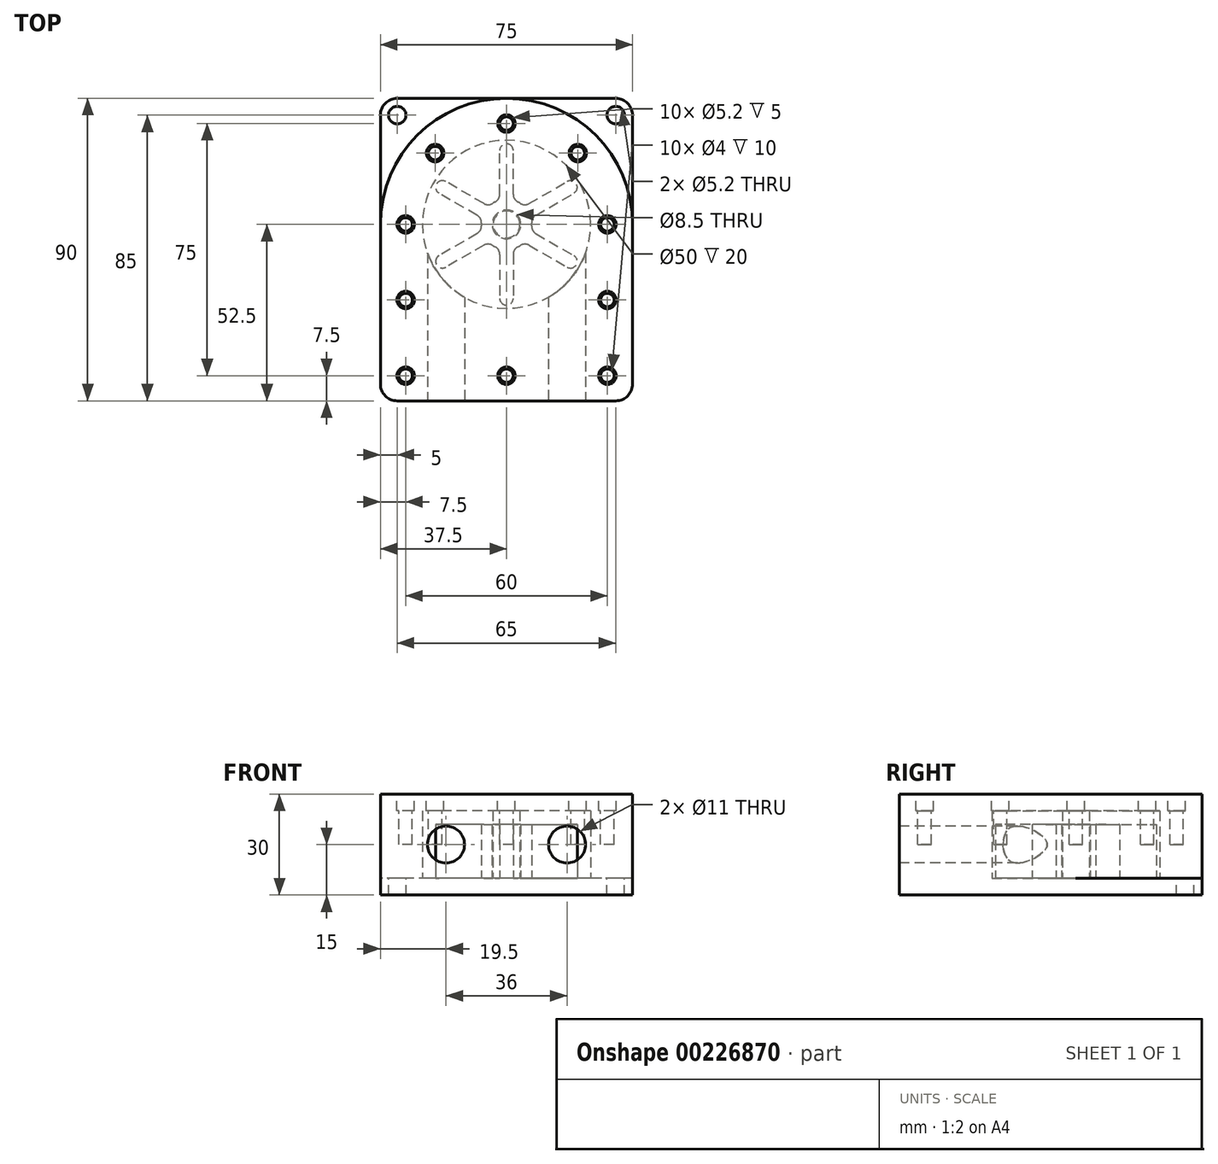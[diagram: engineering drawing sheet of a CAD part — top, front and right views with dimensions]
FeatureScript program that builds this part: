
annotation { "Feature Type Name" : "Feature", "Feature Type Description" : "" }
export const myFeature = defineFeature(function(context is Context, id is Id, definition is map)
    precondition{}
    {
        {
            var Q0;
            Q0=qCreatedBy(makeId("Top.planeOp"),FACE);
            var sketch = newSketch(context, id + "F0", { "sketchPlane" : qUnion([Q0])});
            skCircle(sketch, "E0", {"center": v(0, 0) * mm, "radius": 37.5 * mm});
            skLineSegment(sketch, "E1.bottom", {"start": v(32.5, 37.5) * mm, "end": v(-32.5, 37.5) * mm});
            skLineSegment(sketch, "E1.left", {"start": v(37.5, 32.5) * mm, "end": v(37.5, -37.5) * mm});
            skLineSegment(sketch, "E1.right", {"start": v(-37.5, 32.5) * mm, "end": v(-37.5, -37.5) * mm});
            skLineSegment(sketch, "E2.top", {"start": v(-37.5, -52.5) * mm, "end": v(37.5, -52.5) * mm});
            skLineSegment(sketch, "E2.left", {"start": v(-37.5, -37.5) * mm, "end": v(-37.5, -52.5) * mm});
            skLineSegment(sketch, "E2.right", {"start": v(37.5, -37.5) * mm, "end": v(37.5, -52.5) * mm});
            skPoint(sketch, "E3.visualSharp", {"position": v(-37.5, 37.5) * mm});
            skArc(sketch, "E3.filletArc", {"start": v(-32.5, 37.5) * mm, "mid": v(-36.04, 36.04) * mm, "end": v(-37.5, 32.5) * mm});
            skPoint(sketch, "E4.visualSharp", {"position": v(37.5, 37.5) * mm});
            skArc(sketch, "E4.filletArc", {"start": v(37.5, 32.5) * mm, "mid": v(36.04, 36.04) * mm, "end": v(32.5, 37.5) * mm});
            skCircle(sketch, "E5", {"center": v(-32.5, 32.5) * mm, "radius": 2.6 * mm});
            skCircle(sketch, "E6", {"center": v(32.5, 32.5) * mm, "radius": 2.6 * mm});
            skCircle(sketch, "E7", {"center": v(0, 0) * mm, "radius": 25 * mm});
            skSolve(sketch);
        }
        {
            var Q0;
            {var subQ0=sQuery(id+"F0.wireOp",EDGE,"E4.filletArc");Q0=makeQuery(id+"F0.imprint","IMPRINT",FACE,{"disambiguationData":[TD([[makeQuery(id+"F0.imprint","IMPRINT",EDGE,{"derivedFrom":subQ0}),1.0]])]});}
            var Q1;
            {var subQ0=sQuery(id+"F0.wireOp",EDGE,"E3.filletArc");Q1=makeQuery(id+"F0.imprint","IMPRINT",FACE,{"disambiguationData":[TD([[makeQuery(id+"F0.imprint","IMPRINT",EDGE,{"derivedFrom":subQ0}),1.0]])]});}
            var Q2;
            Q2=makeQuery(id+"F0.imprint","IMPRINT",FACE,{"disambiguationData":[TD([[makeQuery(id+"F0.imprint","IMPRINT",EDGE,{"derivedFrom":sQuery(id+"F0.wireOp",EDGE,"E2.top")}),1.0]])]});
            var Q3;
            {var subQ0=sQuery(id+"F0.wireOp",EDGE,"E0");var subQ1=makeQuery(id+"F0.imprint","INTERSECT",VERTEX,{"derivedFrom":[subQ0,sQuery(id+"F0.wireOp",EDGE,"E1.bottom")]});Q3=makeQuery(id+"F0.imprint","IMPRINT",FACE,{"disambiguationData":[TD([[makeQuery(id+"F0.imprint","IMPRINT",EDGE,{"disambiguationData":[TD([[subQ1,1.0]])],"derivedFrom":subQ0}),1.0]])]});}
            var Q4;
            Q4=makeQuery(id+"F0.imprint","IMPRINT",FACE,{"disambiguationData":[TD([[makeQuery(id+"F0.imprint","IMPRINT",EDGE,{"derivedFrom":sQuery(id+"F0.wireOp",EDGE,"E7")}),1.0]])]});
            extrude(context, id + "F1", {"entities" : qUnion([Q0, Q1, Q2, Q3, Q4]), "oppositeDirection" : true, "depth" : 5 * mm});
        }
        {
            var Q0;
            Q0=makeQuery(id+"F0.imprint","IMPRINT",FACE,{"disambiguationData":[TD([[makeQuery(id+"F0.imprint","IMPRINT",EDGE,{"derivedFrom":sQuery(id+"F0.wireOp",EDGE,"E7")}),-1.0]])]});
            var Q1;
            Q1=makeQuery(id+"F0.imprint","IMPRINT",FACE,{"disambiguationData":[TD([[makeQuery(id+"F0.imprint","IMPRINT",EDGE,{"derivedFrom":sQuery(id+"F0.wireOp",EDGE,"E2.top")}),1.0]])]});
            extrude(context, id + "F2", {"entities" : qUnion([Q0, Q1]), "operationType" : NewBodyOperationType.ADD, "depth" : 20 * mm});
        }
        {
            var Q0;
            Q0=makeQuery(id+"F2.opExtrude","CAP_FACE",FACE,{"disambiguationData":[OSD([sQuery(id+"F0.wireOp",EDGE,"E0"),sQuery(id+"F0.wireOp",EDGE,"E1.left"),sQuery(id+"F0.wireOp",EDGE,"E1.right"),sQuery(id+"F0.wireOp",EDGE,"E2.top"),sQuery(id+"F0.wireOp",EDGE,"E2.left"),sQuery(id+"F0.wireOp",EDGE,"E2.right"),sQuery(id+"F0.wireOp",EDGE,"E7")])],"isStart":false});
            var sketch = newSketch(context, id + "F3", { "sketchPlane" : qUnion([Q0])});
            skArc(sketch, "E8.0.0", {"start": v(37.5, 0) * mm, "mid": v(0, 37.5) * mm, "end": v(-37.5, 0) * mm});
            skLineSegment(sketch, "E8.0.1", {"start": v(-37.5, 0) * mm, "end": v(-37.5, -52.5) * mm});
            skLineSegment(sketch, "E8.0.2", {"start": v(-37.5, -52.5) * mm, "end": v(37.5, -52.5) * mm});
            skLineSegment(sketch, "E8.0.3", {"start": v(37.5, -52.5) * mm, "end": v(37.5, 0) * mm});
            skSolve(sketch);
        }
        {
            var Q0;
            Q0=makeQuery(id+"F3.imprint","IMPRINT",FACE,{"disambiguationData":[TD([[makeQuery(id+"F3.imprint","IMPRINT",EDGE,{"derivedFrom":makeQuery(id+"F2.opExtrude","CAP_EDGE",EDGE,{"disambiguationData":[OSD([sQuery(id+"F0.wireOp",EDGE,"E7")])],"isStart":false})}),1.0]])]});
            var Q1;
            Q1=makeQuery(id+"F3.imprint","IMPRINT",FACE,{"disambiguationData":[TD([[makeQuery(id+"F3.imprint","IMPRINT",EDGE,{"derivedFrom":sQuery(id+"F3.wireOp",EDGE,"E8.0.0")}),1.0]])]});
            extrude(context, id + "F4", {"entities" : qUnion([Q0, Q1]), "depth" : 5 * mm});
        }
        {
            var Q0;
            {var subQ0=sQuery(id+"F0.wireOp",EDGE,"E2.left");var subQ1=sQuery(id+"F0.wireOp",EDGE,"E2.top");Q0=makeQuery(id+"F2.boolean.opBoolean","MERGE",EDGE,{"derivedFrom":[makeQuery(id+"F1.opExtrude","SWEPT_EDGE",EDGE,{"disambiguationData":[OSD([subQ1,subQ0])]}),makeQuery(id+"F2.opExtrude","SWEPT_EDGE",EDGE,{"disambiguationData":[OSD([subQ1,subQ0])]})]});}
            var Q1;
            Q1=makeQuery(id+"F4.opExtrude","SWEPT_EDGE",EDGE,{"disambiguationData":[OSD([sQuery(id+"F3.wireOp",EDGE,"E8.0.1"),sQuery(id+"F3.wireOp",EDGE,"E8.0.2")])]});
            var Q2;
            {var subQ0=sQuery(id+"F0.wireOp",EDGE,"E2.right");var subQ1=sQuery(id+"F0.wireOp",EDGE,"E2.top");Q2=makeQuery(id+"F2.boolean.opBoolean","MERGE",EDGE,{"derivedFrom":[makeQuery(id+"F1.opExtrude","SWEPT_EDGE",EDGE,{"disambiguationData":[OSD([subQ1,subQ0])]}),makeQuery(id+"F2.opExtrude","SWEPT_EDGE",EDGE,{"disambiguationData":[OSD([subQ1,subQ0])]})]});}
            var Q3;
            Q3=makeQuery(id+"F4.opExtrude","SWEPT_EDGE",EDGE,{"disambiguationData":[OSD([sQuery(id+"F3.wireOp",EDGE,"E8.0.2"),sQuery(id+"F3.wireOp",EDGE,"E8.0.3")])]});
            fillet(context, id + "F5", {"entities" : qUnion([Q0, Q1, Q2, Q3]), "radius" : 5 * mm, "tangentPropagation" : true, "allowEdgeOverflow" : false});
        }
        {
            var Q0;
            Q0=makeQuery(id+"F4.opExtrude","CAP_FACE",FACE,{"disambiguationData":[OSD([sQuery(id+"F3.wireOp",EDGE,"E8.0.0"),sQuery(id+"F3.wireOp",EDGE,"E8.0.1"),sQuery(id+"F3.wireOp",EDGE,"E8.0.2"),sQuery(id+"F3.wireOp",EDGE,"E8.0.3")])],"isStart":false});
            var sketch = newSketch(context, id + "F6", { "sketchPlane" : qUnion([Q0])});
            skCircle(sketch, "E9", {"center": v(0, 0) * mm, "radius": 30 * mm, "construction": true});
            skLineSegment(sketch, "E10.bottom", {"start": v(-30, 0) * mm, "end": v(30, 0) * mm, "construction": true});
            skLineSegment(sketch, "E10.top", {"start": v(-30, -45) * mm, "end": v(30, -45) * mm, "construction": true});
            skLineSegment(sketch, "E10.left", {"start": v(-30, 0) * mm, "end": v(-30, -45) * mm, "construction": true});
            skLineSegment(sketch, "E10.right", {"start": v(30, 0) * mm, "end": v(30, -45) * mm, "construction": true});
            skCircle(sketch, "E11", {"center": v(-30, -45) * mm, "radius": 2 * mm});
            skCircle(sketch, "E12", {"center": v(30, -45) * mm, "radius": 2 * mm});
            skCircle(sketch, "E13", {"center": v(0, -45) * mm, "radius": 2 * mm});
            skCircle(sketch, "E14", {"center": v(-30, 0) * mm, "radius": 2 * mm});
            skCircle(sketch, "E15", {"center": v(30, 0) * mm, "radius": 2 * mm});
            skCircle(sketch, "E16", {"center": v(30, -22.5) * mm, "radius": 2 * mm});
            skPoint(sketch, "E16.perimeterSnap0", {"position": v(30, -22.5) * mm});
            skCircle(sketch, "E17", {"center": v(-30, -22.5) * mm, "radius": 2 * mm});
            skCircle(sketch, "E18", {"center": v(0, 30) * mm, "radius": 2 * mm});
            skLineSegment(sketch, "E19", {"start": v(0, 0) * mm, "end": v(-21.21, 21.21) * mm, "construction": true});
            skLineSegment(sketch, "E20", {"start": v(0, 0) * mm, "end": v(21.21, 21.21) * mm, "construction": true});
            skCircle(sketch, "E21", {"center": v(-21.21, 21.21) * mm, "radius": 2 * mm});
            skCircle(sketch, "E22", {"center": v(21.21, 21.21) * mm, "radius": 2 * mm});
            skSolve(sketch);
        }
        {
            var Q0;
            Q0 = qSketchRegion(id + "F6", true);
            extrude(context, id + "F7", {"entities" : qUnion([Q0]), "operationType" : NewBodyOperationType.REMOVE, "oppositeDirection" : true, "depth" : 15 * mm});
        }
        {
            var Q0;
            Q0=qCreatedBy(makeId("Top.planeOp"),FACE);
            var sketch = newSketch(context, id + "F8", { "sketchPlane" : qUnion([Q0])});
            skCircle(sketch, "E23", {"center": v(0, 0) * mm, "radius": 4 * mm});
            skSolve(sketch);
        }
        {
            var Q0;
            Q0=makeQuery(id+"F8.imprint","IMPRINT",FACE,{"disambiguationData":[TD([[makeQuery(id+"F8.imprint","IMPRINT",EDGE,{"derivedFrom":sQuery(id+"F8.wireOp",EDGE,"E23")}),1.0]])]});
            extrude(context, id + "F9", {"entities" : qUnion([Q0]), "operationType" : NewBodyOperationType.ADD, "depth" : 20 * mm});
        }
        {
            var Q0;
            Q0=makeQuery(id+"F4.opExtrude","CAP_FACE",FACE,{"disambiguationData":[OSD([sQuery(id+"F3.wireOp",EDGE,"E8.0.0"),sQuery(id+"F3.wireOp",EDGE,"E8.0.1"),sQuery(id+"F3.wireOp",EDGE,"E8.0.2"),sQuery(id+"F3.wireOp",EDGE,"E8.0.3")])],"isStart":false});
            var sketch = newSketch(context, id + "F10", { "sketchPlane" : qUnion([Q0])});
            skCircle(sketch, "E24", {"center": v(-30, -45) * mm, "radius": 2.6 * mm});
            skCircle(sketch, "E25", {"center": v(0, -45) * mm, "radius": 2.6 * mm});
            skCircle(sketch, "E26", {"center": v(-30, -22.5) * mm, "radius": 2.6 * mm});
            skCircle(sketch, "E27", {"center": v(30, -45) * mm, "radius": 2.6 * mm});
            skCircle(sketch, "E28", {"center": v(30, -22.5) * mm, "radius": 2.6 * mm});
            skCircle(sketch, "E29", {"center": v(30, 0) * mm, "radius": 2.6 * mm});
            skCircle(sketch, "E30", {"center": v(21.21, 21.21) * mm, "radius": 2.6 * mm});
            skCircle(sketch, "E31", {"center": v(0, 30) * mm, "radius": 2.6 * mm});
            skCircle(sketch, "E32", {"center": v(-21.21, 21.21) * mm, "radius": 2.6 * mm});
            skCircle(sketch, "E33", {"center": v(-30, 0) * mm, "radius": 2.6 * mm});
            skSolve(sketch);
        }
        {
            var Q0;
            Q0 = qSketchRegion(id + "F10", true);
            extrude(context, id + "F11", {"entities" : qUnion([Q0]), "operationType" : NewBodyOperationType.REMOVE, "oppositeDirection" : true, "depth" : 5 * mm});
        }
        {
            var Q0;
            {var subQ0=sQuery(id+"F0.wireOp",EDGE,"E2.top");Q0=makeQuery(id+"F2.boolean.opBoolean","MERGE",FACE,{"derivedFrom":[makeQuery(id+"F1.opExtrude","SWEPT_FACE",FACE,{"disambiguationData":[OSD([subQ0])]}),makeQuery(id+"F2.opExtrude","SWEPT_FACE",FACE,{"disambiguationData":[OSD([subQ0])]})]});}
            var sketch = newSketch(context, id + "F12", { "sketchPlane" : qUnion([Q0])});
            skLineSegment(sketch, "E34", {"start": v(-52.85, 10) * mm, "end": v(52.13, 10) * mm, "construction": true});
            skCircle(sketch, "E35", {"center": v(-18, 10) * mm, "radius": 5.5 * mm});
            skCircle(sketch, "E36", {"center": v(18, 10) * mm, "radius": 5.5 * mm});
            skSolve(sketch);
        }
        {
            var Q0;
            Q0=makeQuery(id+"F12.imprint","IMPRINT",FACE,{"disambiguationData":[TD([[makeQuery(id+"F12.imprint","IMPRINT",EDGE,{"derivedFrom":sQuery(id+"F12.wireOp",EDGE,"E35")}),1.0]])]});
            var Q1;
            Q1=makeQuery(id+"F12.imprint","IMPRINT",FACE,{"disambiguationData":[TD([[makeQuery(id+"F12.imprint","IMPRINT",EDGE,{"derivedFrom":sQuery(id+"F12.wireOp",EDGE,"E36")}),1.0]])]});
            extrude(context, id + "F13", {"entities" : qUnion([Q0, Q1]), "operationType" : NewBodyOperationType.REMOVE, "oppositeDirection" : true, "depth" : 50 * mm});
        }
        {
            var Q0;
            {var subQ0=sQuery(id+"F0.wireOp",EDGE,"E3.filletArc");Q0=makeQuery(id+"F0.imprint","IMPRINT",FACE,{"disambiguationData":[TD([[makeQuery(id+"F0.imprint","IMPRINT",EDGE,{"derivedFrom":subQ0}),1.0]])]});}
            var sketch = newSketch(context, id + "F14", { "sketchPlane" : qUnion([Q0])});
            skCircle(sketch, "E37", {"center": v(0, 0) * mm, "radius": 4.25 * mm});
            skLineSegment(sketch, "E38", {"start": v(0, 0) * mm, "end": v(0, 22) * mm});
            skArc(sketch, "E39.0.endCap", {"start": v(-2, 22) * mm, "mid": v(0, 24) * mm, "end": v(2, 22) * mm});
            skLineSegment(sketch, "E39.0.left", {"start": v(-2, 8.93) * mm, "end": v(-2, 22) * mm});
            skLineSegment(sketch, "E39.0.right", {"start": v(2, 8.93) * mm, "end": v(2, 22) * mm});
            skArc(sketch, "E40", {"start": v(-3.38, 6.7) * mm, "mid": v(-3.75, 6.5) * mm, "end": v(-4.11, 6.27) * mm});
            skPoint(sketch, "E41.visualSharp", {"position": v(2, 7.23) * mm});
            skArc(sketch, "E41.filletArc", {"start": v(2, 8.93) * mm, "mid": v(2.37, 7.62) * mm, "end": v(3.38, 6.7) * mm});
            skPoint(sketch, "E42.visualSharp", {"position": v(-2, 7.23) * mm});
            skArc(sketch, "E42.filletArc", {"start": v(-3.38, 6.7) * mm, "mid": v(-2.37, 7.62) * mm, "end": v(-2, 8.93) * mm});
            skArc(sketch, "E43.1.0", {"start": v(-20.05, 9.27) * mm, "mid": v(-20.78, 12) * mm, "end": v(-18.05, 12.73) * mm});
            skLineSegment(sketch, "E43.1.1", {"start": v(-8.73, 2.73) * mm, "end": v(-20.05, 9.27) * mm});
            skLineSegment(sketch, "E43.1.2", {"start": v(-6.73, 6.2) * mm, "end": v(-18.05, 12.73) * mm});
            skPoint(sketch, "E43.1.3", {"position": v(-5.26, 5.35) * mm});
            skPoint(sketch, "E43.1.4", {"position": v(-7.26, 1.88) * mm});
            skArc(sketch, "E43.1.5", {"start": v(-6.73, 6.2) * mm, "mid": v(-5.41, 5.86) * mm, "end": v(-4.11, 6.27) * mm});
            skArc(sketch, "E43.1.6", {"start": v(-7.49, 0.43) * mm, "mid": v(-7.78, 1.76) * mm, "end": v(-8.73, 2.73) * mm});
            skArc(sketch, "E43.2.0", {"start": v(-18.05, -12.73) * mm, "mid": v(-20.78, -12) * mm, "end": v(-20.05, -9.27) * mm});
            skLineSegment(sketch, "E43.2.1", {"start": v(-6.73, -6.2) * mm, "end": v(-18.05, -12.73) * mm});
            skLineSegment(sketch, "E43.2.2", {"start": v(-8.73, -2.73) * mm, "end": v(-20.05, -9.27) * mm});
            skPoint(sketch, "E43.2.3", {"position": v(-7.26, -1.88) * mm});
            skPoint(sketch, "E43.2.4", {"position": v(-5.26, -5.35) * mm});
            skArc(sketch, "E43.2.5", {"start": v(-8.73, -2.73) * mm, "mid": v(-7.78, -1.76) * mm, "end": v(-7.49, -0.43) * mm});
            skArc(sketch, "E43.2.6", {"start": v(-4.11, -6.27) * mm, "mid": v(-5.41, -5.86) * mm, "end": v(-6.73, -6.2) * mm});
            skArc(sketch, "E43.3.0", {"start": v(2, -22) * mm, "mid": v(0, -24) * mm, "end": v(-2, -22) * mm});
            skLineSegment(sketch, "E43.3.1", {"start": v(2, -8.93) * mm, "end": v(2, -22) * mm});
            skLineSegment(sketch, "E43.3.2", {"start": v(-2, -8.93) * mm, "end": v(-2, -22) * mm});
            skPoint(sketch, "E43.3.3", {"position": v(-2, -7.23) * mm});
            skPoint(sketch, "E43.3.4", {"position": v(2, -7.23) * mm});
            skArc(sketch, "E43.3.5", {"start": v(-2, -8.93) * mm, "mid": v(-2.37, -7.62) * mm, "end": v(-3.38, -6.7) * mm});
            skArc(sketch, "E43.3.6", {"start": v(3.37, -6.7) * mm, "mid": v(2.37, -7.62) * mm, "end": v(2, -8.93) * mm});
            skArc(sketch, "E43.4.0", {"start": v(20.05, -9.27) * mm, "mid": v(20.78, -12) * mm, "end": v(18.05, -12.73) * mm});
            skLineSegment(sketch, "E43.4.1", {"start": v(8.73, -2.73) * mm, "end": v(20.05, -9.27) * mm});
            skLineSegment(sketch, "E43.4.2", {"start": v(6.73, -6.2) * mm, "end": v(18.05, -12.73) * mm});
            skPoint(sketch, "E43.4.3", {"position": v(5.26, -5.35) * mm});
            skPoint(sketch, "E43.4.4", {"position": v(7.26, -1.88) * mm});
            skArc(sketch, "E43.4.5", {"start": v(6.73, -6.2) * mm, "mid": v(5.41, -5.86) * mm, "end": v(4.11, -6.27) * mm});
            skArc(sketch, "E43.4.6", {"start": v(7.49, -0.43) * mm, "mid": v(7.78, -1.76) * mm, "end": v(8.73, -2.73) * mm});
            skArc(sketch, "E43.5.0", {"start": v(18.05, 12.73) * mm, "mid": v(20.78, 12) * mm, "end": v(20.05, 9.27) * mm});
            skLineSegment(sketch, "E43.5.1", {"start": v(6.73, 6.2) * mm, "end": v(18.05, 12.73) * mm});
            skLineSegment(sketch, "E43.5.2", {"start": v(8.73, 2.73) * mm, "end": v(20.05, 9.27) * mm});
            skPoint(sketch, "E43.5.3", {"position": v(7.26, 1.88) * mm});
            skPoint(sketch, "E43.5.4", {"position": v(5.26, 5.35) * mm});
            skArc(sketch, "E43.5.5", {"start": v(8.73, 2.73) * mm, "mid": v(7.78, 1.76) * mm, "end": v(7.49, 0.43) * mm});
            skArc(sketch, "E43.5.6", {"start": v(4.11, 6.27) * mm, "mid": v(5.41, 5.86) * mm, "end": v(6.73, 6.2) * mm});
            skArc(sketch, "E44.trimOffspring", {"start": v(4.11, 6.27) * mm, "mid": v(3.75, 6.5) * mm, "end": v(3.37, 6.7) * mm});
            skArc(sketch, "E45.trimOffspring", {"start": v(7.49, -0.43) * mm, "mid": v(7.5, 0) * mm, "end": v(7.49, 0.43) * mm});
            skArc(sketch, "E46.trimOffspring", {"start": v(3.38, -6.7) * mm, "mid": v(3.75, -6.5) * mm, "end": v(4.11, -6.27) * mm});
            skArc(sketch, "E47.trimOffspring", {"start": v(-4.11, -6.27) * mm, "mid": v(-3.75, -6.5) * mm, "end": v(-3.38, -6.7) * mm});
            skArc(sketch, "E48.trimOffspring", {"start": v(-7.49, 0.43) * mm, "mid": v(-7.5, 0) * mm, "end": v(-7.49, -0.43) * mm});
            skSolve(sketch);
        }
        {
            var Q0;
            Q0 = qSketchRegion(id + "F14", true);
            extrude(context, id + "F15", {"entities" : qUnion([Q0]), "depth" : 16 * mm});
        }
    });
